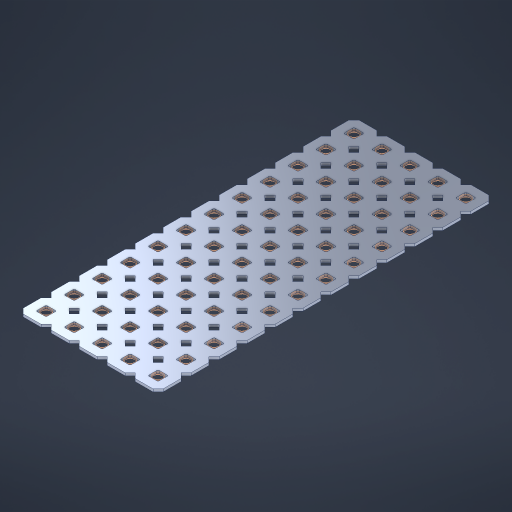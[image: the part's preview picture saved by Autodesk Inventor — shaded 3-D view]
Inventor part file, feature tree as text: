
AUTODESK INVENTOR PART (.ipt)
format: ipt  version: 2023 (Build 270158000, 158)  size: 958,464 bytes
history: native  units: in
note: dims shown in document units (in); Inventor stores cm internally (conversion verified against a paired STEP export)
features: other x61, extrude x59, sketch x2, pattern_linear x1
ambient origin geometry x8: Origin, YZ Plane, XZ Plane, XY Plane, X Axis, Y Axis, Z Axis, Center Point
bodies: Solid1 (feature_tree), Body (feature_tree)
feature tree (123):
  pattern_linear  "Rectangular Pattern1"  Spacing1=0.09in  [1 undecoded]
  sketch  "Sketch1"  dims[d1=0.5in]
  sketch  "Sketch2"  dims[d2=0.182in d3=0.09in d4=0.09in d5=0.09in d6=0.09in d7=0.09in d8=0.09in d9=0.09in d10=0.09in d11=0.02in d13=0.0in d14=0.172in d15=0.0625in d16=0.0in d19=0.5in d22=0.5in]
  other  "Srf1"
  other  "Srf126"
  other  "Srf127"
  other  "Srf128"
  other  "Srf129"
  other  "Srf130"
  other  "Srf131"
  other  "Srf250"
  other  "Srf251"
  other  "Srf252"
  other  "Srf253"
  other  "Srf254"
  other  "Srf268"
  other  "Srf269"
  other  "Srf270"
  other  "Srf271"
  other  "Srf272"
  other  "Srf273"
  other  "Srf274"
  other  "Srf275"
  other  "Srf276"
  other  "Srf277"
  other  "Srf278"
  other  "Srf279"
  other  "Srf293"
  other  "Srf294"
  other  "Srf295"
  other  "Srf296"
  other  "Srf297"
  other  "Srf298"
  other  "Srf299"
  other  "Srf300"
  other  "Srf301"
  other  "Srf302"
  other  "Srf303"
  other  "Srf304"
  other  "Srf318"
  other  "Srf319"
  other  "Srf320"
  other  "Srf321"
  other  "Srf322"
  other  "Srf323"
  other  "Srf324"
  other  "Srf325"
  other  "Srf326"
  other  "Srf327"
  other  "Srf328"
  other  "Srf329"
  other  "Srf343"
  other  "Srf344"
  other  "Srf345"
  other  "Srf346"
  other  "Srf347"
  other  "Srf348"
  other  "Srf349"
  other  "Srf350"
  other  "Srf351"
  other  "Srf352"
  other  "Srf353"
  other  "Srf354"
  other  "Circle"
  extrude  "ExtrusionSrf126"  Depth=0.09in
  extrude  "ExtrusionSrf127"  Depth=0.09in
  extrude  "ExtrusionSrf128"  Depth=0.09in
  extrude  "ExtrusionSrf129"  Depth=0.09in
  extrude  "ExtrusionSrf130"  Depth=0.09in
  extrude  "ExtrusionSrf131"  Depth=0.09in
  extrude  "ExtrusionSrf250"  Depth=0.09in
  extrude  "ExtrusionSrf251"  Depth=0.02in
  extrude  "ExtrusionSrf252"  TaperAngle=0.0deg  [1 undecoded]
  extrude  "ExtrusionSrf253"  Depth=0.5in
  extrude  "ExtrusionSrf254"  Depth=0.5in TaperAngle=0.0deg
  extrude  "ExtrusionSrf268"  Depth=0.5in
  extrude  "ExtrusionSrf269"  Depth=0.5in
  extrude  "ExtrusionSrf270"  [1 undecoded]
  extrude  "ExtrusionSrf271"  [1 undecoded]
  extrude  "ExtrusionSrf272"  [1 undecoded]
  extrude  "ExtrusionSrf273"  [1 undecoded]
  extrude  "ExtrusionSrf274"  [1 undecoded]
  extrude  "ExtrusionSrf275"  [1 undecoded]
  extrude  "ExtrusionSrf276"  [1 undecoded]
  extrude  "ExtrusionSrf277"  [1 undecoded]
  extrude  "ExtrusionSrf278"  [1 undecoded]
  extrude  "ExtrusionSrf279"  [1 undecoded]
  extrude  "ExtrusionSrf293"  [1 undecoded]
  extrude  "ExtrusionSrf294"  [1 undecoded]
  extrude  "ExtrusionSrf295"  [1 undecoded]
  extrude  "ExtrusionSrf296"  [1 undecoded]
  extrude  "ExtrusionSrf297"  [1 undecoded]
  extrude  "ExtrusionSrf298"  [1 undecoded]
  extrude  "ExtrusionSrf299"  [1 undecoded]
  extrude  "ExtrusionSrf300"  [1 undecoded]
  extrude  "ExtrusionSrf301"  [1 undecoded]
  extrude  "ExtrusionSrf302"  [1 undecoded]
  extrude  "ExtrusionSrf303"  [1 undecoded]
  extrude  "ExtrusionSrf304"  [1 undecoded]
  extrude  "ExtrusionSrf318"  [1 undecoded]
  extrude  "ExtrusionSrf319"  [1 undecoded]
  extrude  "ExtrusionSrf320"  [1 undecoded]
  extrude  "ExtrusionSrf321"  [1 undecoded]
  extrude  "ExtrusionSrf322"  [1 undecoded]
  extrude  "ExtrusionSrf323"  [1 undecoded]
  extrude  "ExtrusionSrf324"  [1 undecoded]
  extrude  "ExtrusionSrf325"  [1 undecoded]
  extrude  "ExtrusionSrf326"  [1 undecoded]
  extrude  "ExtrusionSrf327"  [1 undecoded]
  extrude  "ExtrusionSrf328"  [1 undecoded]
  extrude  "ExtrusionSrf329"  [1 undecoded]
  extrude  "ExtrusionSrf343"  [1 undecoded]
  extrude  "ExtrusionSrf344"  [1 undecoded]
  extrude  "ExtrusionSrf345"  [1 undecoded]
  extrude  "ExtrusionSrf346"  [1 undecoded]
  extrude  "ExtrusionSrf347"  [1 undecoded]
  extrude  "ExtrusionSrf348"  [1 undecoded]
  extrude  "ExtrusionSrf349"  [1 undecoded]
  extrude  "ExtrusionSrf350"  [1 undecoded]
  extrude  "ExtrusionSrf351"  [1 undecoded]
  extrude  "ExtrusionSrf352"  [1 undecoded]
  extrude  "ExtrusionSrf353"  [1 undecoded]
  extrude  "ExtrusionSrf354"  [1 undecoded]
note: 48 required parameter values undecoded (feature->parameter linkage not recoverable at this tier; creation-order binding heuristic only, values carry confidence <= 0.55)
